# Revit family: Drain-Green_Roof-Jay R. Smith-Round_Type-1935_Series
name_source: partatom
category: Plumbing Fixtures
units: mm (PartAtom-declared; Revit-internal decimal feet)

## family parameters
Always vertical = Yes
Cut with Voids When Loaded = No
OmniClass Number = 23.70.50.21.24.11
OmniClass Title = Roof Waste Water Drains
Part Type = Normal
Room Calculation Point = No
Round Connector Dimension = Use Radius
Shared = No
Work Plane-Based = Yes

## types (15) — shared parameters
AE - Adjustable Extension = No
Assembly Code = D2040200
BZS - Bronze Standpipe = No
Body Material = Cast Iron-Jay R Smith-Duco Coated
C - Underdeck Clamp = No
CIS - Cast Iron Standpipe = No
CL - "L" Shaped Underdeck Clamp = No
CW Connection = No
Default Elevation = 0"
Description = Green Roof Planter Drain Basin
Dome Material = PVC-Jay R Smith-White
E - Extension (specify height) = No
Expansion Joint (Specify Fig. 1710) = No
G - Galvanized Cast Iron = No
Gravel Guard Material = Stainless Steel-Jay R Smith-Perforated
HW Connection = No
Installation Type = Roof Mounted
L - Speedi-Set Service Weight - 02"(50), 03"(75) & 04"(100) sizes only = No
LXH - Speedi-Set Extra Heavy - 02"(50), 03"(75) & 04"(100) sizes only = No
Manufacturer = Jay R. Smith
Material = Cast Iron-Jay R Smith-Duco Coated
Overall Diameter = 20"
Perforated Gravel Stop Height = 12"
Perforated P.V.C. Standpipe Height = 2"
Product Documentation Link = https://www.jrsmith.com
Product Page URL = https://www.jrsmith.com
Standpipe Material = PVC-Jay R Smith-White
T - Threaded Outlet = No
U - Vandal Proof = No
URL = http://www.jrsmith.com
Vent Connection = No
Waste Connection = Yes

## per-type parameters (varying)
| type | B Dimension | B Dimension/2 | Bottom Depth | Connection Description | Outlet Diameter | Outlet Radius |
| 1935C02 | 4" | 2" | 5" | 2" Caulk Outlet Connection | 2" | 1" |
| 1935C03 | 4" | 2" | 5" | 3" Caulk Outlet Connection | 3" | 1 1/2" |
| 1935C04 | 4" | 2" | 5" | 4" Caulk Outlet Connection | 4" | 2" |
| 1935C05 | 6" | 3" | 5" | 5" Caulk Outlet Connection | 5" | 2 1/2" |
| 1935C06 | 6" | 3" | 5" | 6" Caulk Outlet Connection | 6" | 3" |
| 1935Y02 | 4" | 2" | 5" | 2" No-HUB Outlet Connection | 2" | 1" |
| 1935Y03 | 4" | 2" | 5" | 3" No-HUB Outlet Connection | 3" | 1 1/2" |
| 1935Y04 | 4" | 2" | 5" | 4" No-HUB Outlet Connection | 4" | 2" |
| 1935Y05 | 6" | 3" | 5" | 5" No-HUB Outlet Connection | 5" | 2 1/2" |
| 1935Y06 | 6" | 3" | 5" | 6" No-HUB Outlet Connection | 6" | 3" |
| 1935T02 | 4" | 2" | 3 3/4" | 2" Threaded Outlet Connection | 2" | 1" |
| 1935T03 | 4" | 2" | 3 3/4" | 3" Threaded Outlet Connection | 3" | 1 1/2" |
| 1935T04 | 4" | 2" | 3 3/4" | 4" Threaded Outlet Connection | 4" | 2" |
| 1935T05 | 6" | 3" | 3 3/4" | 5" Threaded Outlet Connection | 5" | 2 1/2" |
| 1935T06 | 6" | 3" | 3 3/4" | 6" Threaded Outlet Connection | 6" | 3" |

note: column(s) folded — value = type name in every type: Model

## geometry (parser evidence)
native form markers: Sweep x4
no freeform markers — native parametric forms only
